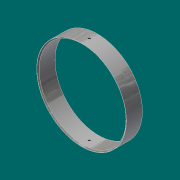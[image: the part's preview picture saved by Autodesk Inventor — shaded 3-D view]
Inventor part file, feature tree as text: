
AUTODESK INVENTOR PART (.ipt)
format: ipt  version: 2017.3 (Build 213257000, 257)  size: 117,248 bytes
history: native  units: in
note: dims shown in document units (in); Inventor stores cm internally (conversion verified against a paired STEP export)
features: chamfer x2, sketch x2, extrude x1, plane x1, hole x1, pattern_circular x1
ambient origin geometry x8: Origin, YZ Plane, XZ Plane, XY Plane, X Axis, Y Axis, Z Axis, Center Point
bodies: Solid1 (feature_tree)
feature tree (8):
  extrude  "Extrusion1"  Depth=31.0in
  chamfer  "Chamfer1"  Distance=6.0394in
  chamfer  "Chamfer2"  Distance=0.125in
  plane  "Work Plane1"
  hole  "Hole1"  [1 undecoded]
  pattern_circular  "Circular Pattern1"  [2 undecoded]
  sketch  "Sketch1"  dims[d0=32.0in d1=31.0in d2=6.0394in d3=0.0in]
  sketch  "Sketch2"  dims[d4=0.4375in d5=0.125in d6=0.2577in d7=0.4375in d8=0.125in d9=0.2749in d10=2.2812in d11=0.891in d12=0.553in d13=0.0246in d14=0.897in d15=0.375in d16=0.25in d17=0.5635in d18=0.91in d19=0.8108in d20=0.7874in d21=360.0deg]
note: 3 required parameter values undecoded (feature->parameter linkage not recoverable at this tier; creation-order binding heuristic only, values carry confidence <= 0.55)
